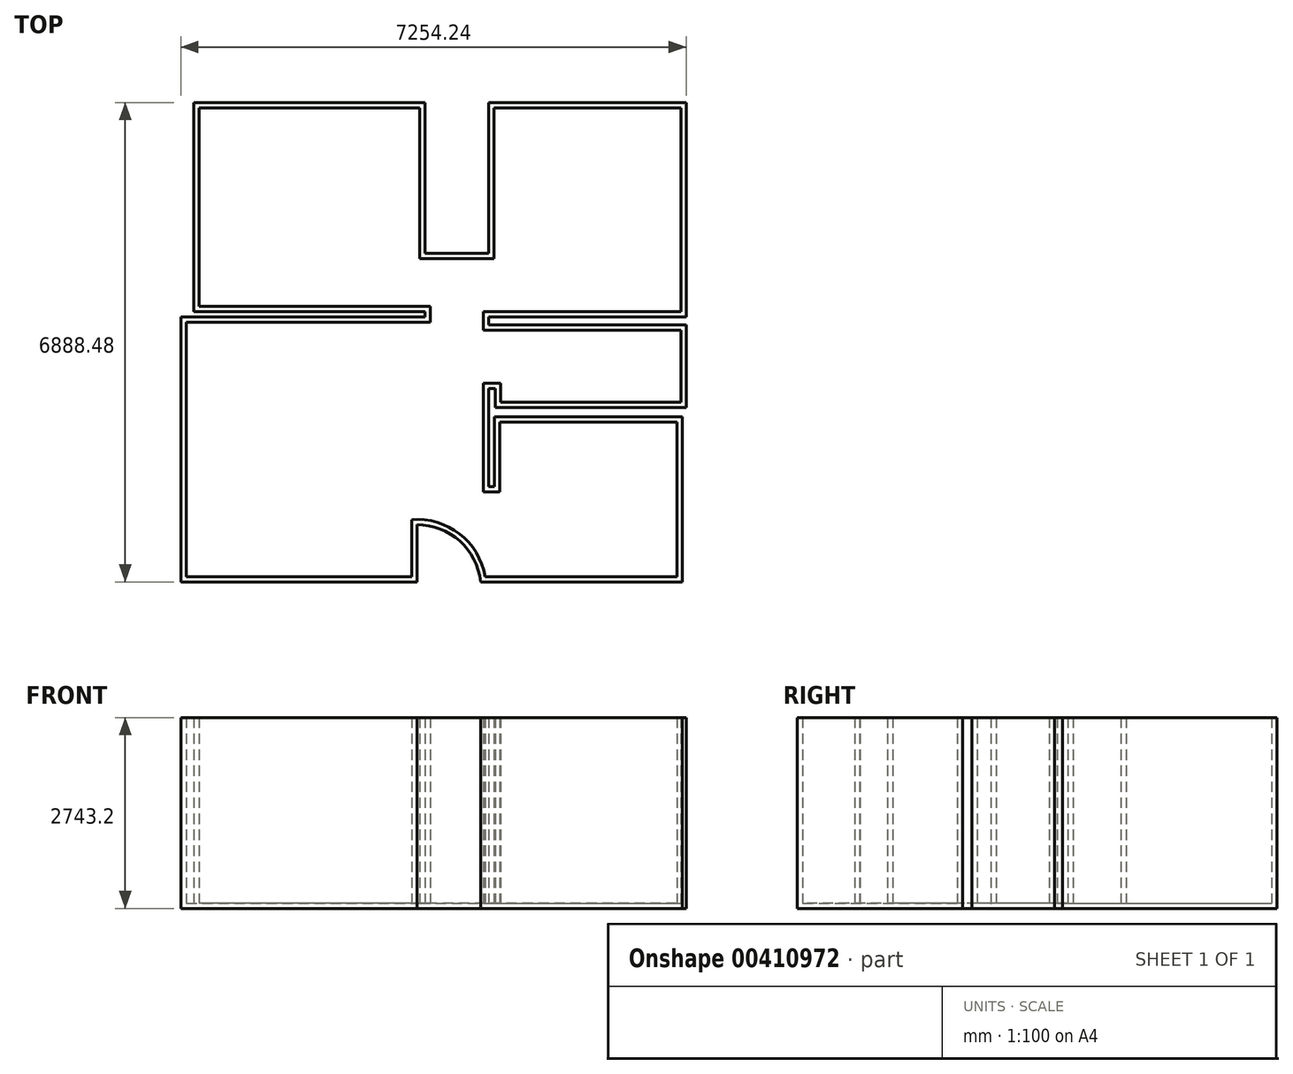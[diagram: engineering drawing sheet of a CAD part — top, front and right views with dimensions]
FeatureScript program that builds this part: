
annotation { "Feature Type Name" : "Feature", "Feature Type Description" : "" }
export const myFeature = defineFeature(function(context is Context, id is Id, definition is map)
    precondition{}
    {
        {
            var Q0;
            Q0=qCreatedBy(makeId("Top.planeOp"),FACE);
            var sketch = newSketch(context, id + "F0", { "sketchPlane" : qUnion([Q0])});
            skLineSegment(sketch, "E0", {"start": v(-1809.84, 3765.21) * mm, "end": v(-1809.84, -44.79) * mm});
            skLineSegment(sketch, "E1", {"start": v(-1809.84, 3765.21) * mm, "end": v(1695.36, 3765.21) * mm});
            skLineSegment(sketch, "E2", {"start": v(-1809.84, -44.79) * mm, "end": v(1578.26, -44.79) * mm});
            skLineSegment(sketch, "E3", {"start": v(5388.26, -44.79) * mm, "end": v(2492.66, -44.79) * mm});
            skLineSegment(sketch, "E4", {"start": v(5388.26, -44.79) * mm, "end": v(5388.26, 1326.81) * mm});
            skLineSegment(sketch, "E5", {"start": v(2609.76, 3765.21) * mm, "end": v(2609.76, 3648.36) * mm});
            skLineSegment(sketch, "E6", {"start": v(2609.76, 2733.96) * mm, "end": v(2609.76, 1326.81) * mm});
            skLineSegment(sketch, "E7", {"start": v(2609.76, 1326.81) * mm, "end": v(2692.05, 1326.81) * mm});
            skLineSegment(sketch, "E8", {"start": v(1695.36, 3765.21) * mm, "end": v(1695.36, 3841.41) * mm});
            skLineSegment(sketch, "E9", {"start": v(1695.36, 4679.61) * mm, "end": v(2609.76, 4679.61) * mm});
            skLineSegment(sketch, "E10.bottom", {"start": v(1695.36, 3765.21) * mm, "end": v(-1626.96, 3765.21) * mm});
            skLineSegment(sketch, "E10.top", {"start": v(1695.36, 6843.7) * mm, "end": v(-1626.96, 6843.7) * mm});
            skLineSegment(sketch, "E10.right", {"start": v(-1626.96, 3841.41) * mm, "end": v(-1626.96, 6843.7) * mm});
            skLineSegment(sketch, "E11.bottom", {"start": v(2609.76, 3765.21) * mm, "end": v(5444.4, 3765.21) * mm});
            skLineSegment(sketch, "E11.top", {"start": v(2609.76, 6843.7) * mm, "end": v(5444.4, 6843.7) * mm});
            skLineSegment(sketch, "E11.left", {"start": v(2609.76, 4679.61) * mm, "end": v(2609.76, 6843.7) * mm});
            skLineSegment(sketch, "E11.right", {"start": v(5444.4, 3765.21) * mm, "end": v(5444.4, 6843.7) * mm});
            skLineSegment(sketch, "E12", {"start": v(1695.36, 3841.41) * mm, "end": v(-1626.96, 3841.41) * mm});
            skLineSegment(sketch, "E13.trimOffspring", {"start": v(1695.36, 4679.61) * mm, "end": v(1695.36, 6843.7) * mm});
            skLineSegment(sketch, "E14", {"start": v(5388.26, 1326.81) * mm, "end": v(5388.26, 2325.43) * mm});
            skLineSegment(sketch, "E15", {"start": v(5388.26, 2325.43) * mm, "end": v(2692.05, 2325.43) * mm});
            skLineSegment(sketch, "E16", {"start": v(2692.05, 2325.43) * mm, "end": v(2692.05, 1326.81) * mm});
            skLineSegment(sketch, "E17", {"start": v(2609.76, 3648.36) * mm, "end": v(5444.4, 3648.36) * mm});
            skLineSegment(sketch, "E18", {"start": v(5444.4, 3648.36) * mm, "end": v(5444.4, 2733.96) * mm});
            skLineSegment(sketch, "E19", {"start": v(2609.76, 2733.96) * mm, "end": v(2703.35, 2733.96) * mm});
            skLineSegment(sketch, "E20", {"start": v(2703.35, 2733.96) * mm, "end": v(2703.35, 2462.9) * mm});
            skLineSegment(sketch, "E21", {"start": v(2703.35, 2462.9) * mm, "end": v(5444.4, 2462.9) * mm});
            skLineSegment(sketch, "E22", {"start": v(5444.4, 2462.9) * mm, "end": v(5444.4, 2733.96) * mm});
            skArc(sketch, "E23", {"start": v(2492.66, -44.79) * mm, "mid": v(2193.73, 541.8) * mm, "end": v(1578.26, 775.57) * mm});
            skLineSegment(sketch, "E24", {"start": v(1578.26, -44.79) * mm, "end": v(1578.26, 775.57) * mm});
            skSolve(sketch);
        }
        {
            var Q0;
            Q0=makeQuery(id+"F0.imprint","IMPRINT",FACE,{"disambiguationData":[TD([[makeQuery(id+"F0.imprint","IMPRINT",EDGE,{"derivedFrom":sQuery(id+"F0.wireOp",EDGE,"E0")}),1.0]])]});
            extrude(context, id + "F1", {"entities" : qUnion([Q0]), "depth" : 2743.2 * mm});
        }
        {
            var Q0;
            Q0=makeQuery(id+"F1.opExtrude","CAP_FACE",FACE,{"disambiguationData":[OSD([sQuery(id+"F0.wireOp",EDGE,"E0"),sQuery(id+"F0.wireOp",EDGE,"E1"),sQuery(id+"F0.wireOp",EDGE,"E2"),sQuery(id+"F0.wireOp",EDGE,"E3"),sQuery(id+"F0.wireOp",EDGE,"E4"),sQuery(id+"F0.wireOp",EDGE,"E5"),sQuery(id+"F0.wireOp",EDGE,"E6"),sQuery(id+"F0.wireOp",EDGE,"E7"),sQuery(id+"F0.wireOp",EDGE,"E9"),sQuery(id+"F0.wireOp",EDGE,"E10.bottom"),sQuery(id+"F0.wireOp",EDGE,"E10.top"),sQuery(id+"F0.wireOp",EDGE,"E8"),sQuery(id+"F0.wireOp",EDGE,"E10.right"),sQuery(id+"F0.wireOp",EDGE,"E11.bottom"),sQuery(id+"F0.wireOp",EDGE,"E11.top"),sQuery(id+"F0.wireOp",EDGE,"E11.left"),sQuery(id+"F0.wireOp",EDGE,"E11.right"),sQuery(id+"F0.wireOp",EDGE,"E12"),sQuery(id+"F0.wireOp",EDGE,"E13.trimOffspring"),sQuery(id+"F0.wireOp",EDGE,"e7aab296-073b-465b-91d3-86c9746a0d38")])],"isStart":false});
            shell(context, id + "F2", {"entities" : qUnion([Q0]), "thickness" : 76.2 * mm});
        }
    });
